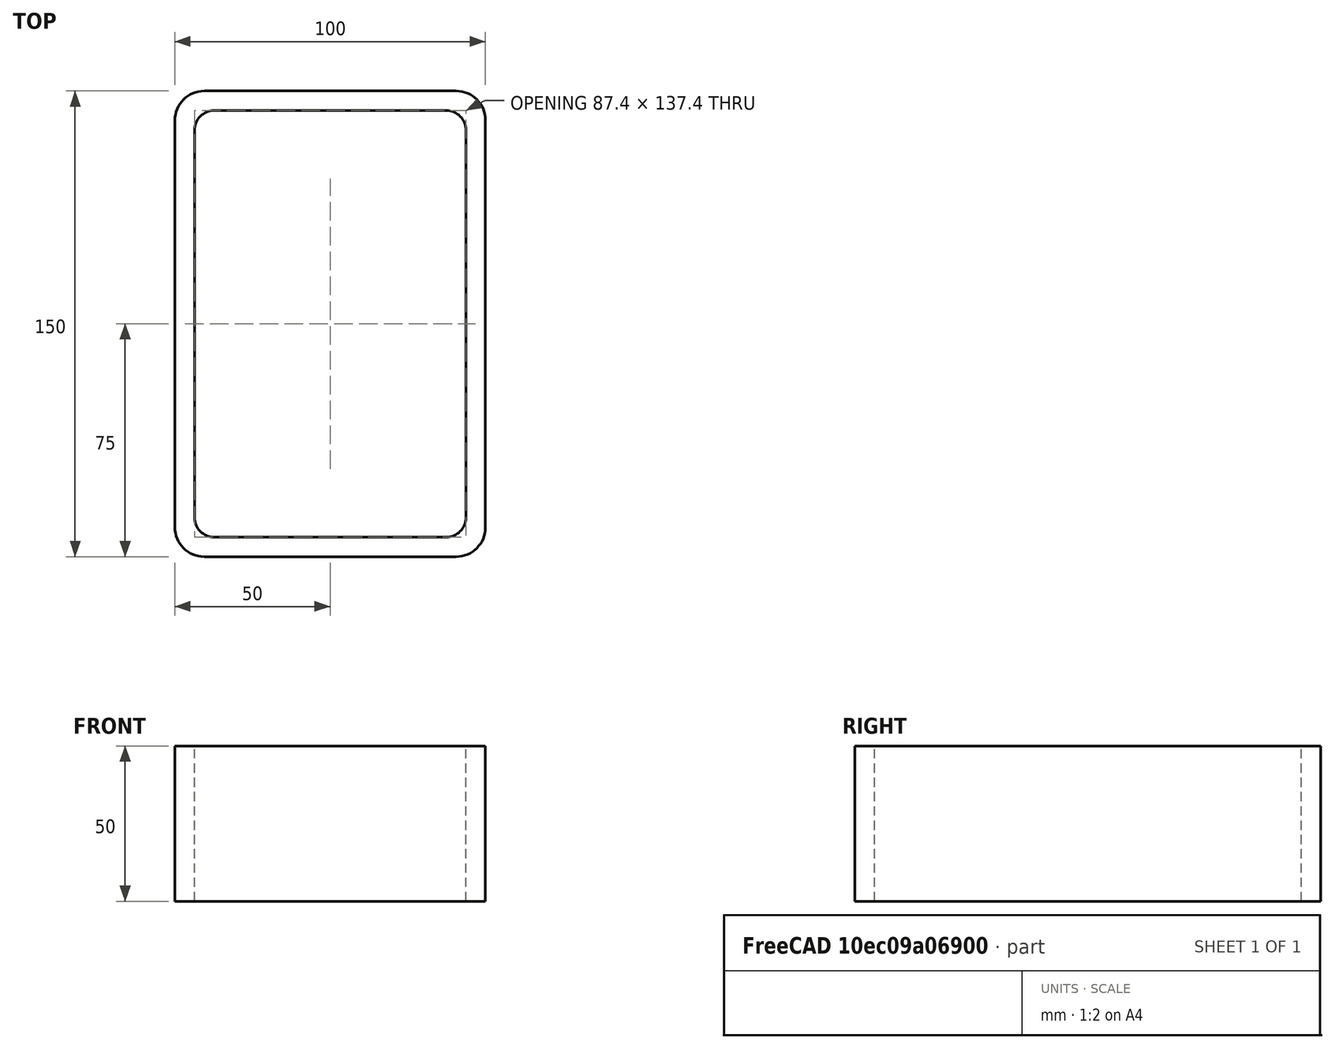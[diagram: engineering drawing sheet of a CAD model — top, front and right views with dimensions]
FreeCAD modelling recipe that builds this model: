
FCSTD DOCUMENT  (FreeCAD 0.15R4671 (Git))
Label: Rectangular hollow section 150x100x6.3 EN10219 S235JRH
License: All rights reserved
LicenseURL: http://en.wikipedia.org/wiki/All_rights_reserved
objects: Sketcher::SketchObject×1, Part::Extrusion×1
note: 2 computed .brp shape members not serialized (recipe doc carries the construction recipe); baked Part::Feature solids carry a one-line shape summary decoded from their .brp

FEATURE [Sketcher::SketchObject] Sketch
  sketch-geometry (16):
    g0: LineSegment StartX=-37.4 StartY=68.7 StartZ=0 EndX=37.4 EndY=68.7 EndZ=0
    g1: LineSegment StartX=43.7 StartY=62.4 StartZ=0 EndX=43.7 EndY=-62.4 EndZ=0
    g2: LineSegment StartX=37.4 StartY=-68.7 StartZ=0 EndX=-37.4 EndY=-68.7 EndZ=0
    g3: LineSegment StartX=-43.7 StartY=-62.4 StartZ=0 EndX=-43.7 EndY=62.4 EndZ=0
    g4: LineSegment StartX=-40.55 StartY=75 StartZ=0 EndX=40.55 EndY=75 EndZ=0
    g5: LineSegment StartX=50 StartY=65.55 StartZ=0 EndX=50 EndY=-65.55 EndZ=0
    g6: LineSegment StartX=40.55 StartY=-75 StartZ=0 EndX=-40.55 EndY=-75 EndZ=0
    g7: LineSegment StartX=-50 StartY=-65.55 StartZ=0 EndX=-50 EndY=65.55 EndZ=0
    g8: ArcOfCircle CenterX=-37.4 CenterY=62.4 CenterZ=0 NormalX=0 NormalY=0 NormalZ=1 Radius=6.3 StartAngle=1.5708 EndAngle=3.14159
    g9: ArcOfCircle CenterX=37.4 CenterY=62.4 CenterZ=0 NormalX=0 NormalY=0 NormalZ=1 Radius=6.3 StartAngle=0 EndAngle=1.5708
    g10: ArcOfCircle CenterX=37.4 CenterY=-62.4 CenterZ=0 NormalX=0 NormalY=0 NormalZ=1 Radius=6.3 StartAngle=4.71239 EndAngle=6.28319
    g11: ArcOfCircle CenterX=-37.4 CenterY=-62.4 CenterZ=0 NormalX=0 NormalY=0 NormalZ=1 Radius=6.3 StartAngle=3.14159 EndAngle=4.71239
    g12: ArcOfCircle CenterX=40.55 CenterY=65.55 CenterZ=0 NormalX=0 NormalY=0 NormalZ=1 Radius=9.45 StartAngle=0 EndAngle=1.5708
    g13: ArcOfCircle CenterX=40.55 CenterY=-65.55 CenterZ=0 NormalX=0 NormalY=0 NormalZ=1 Radius=9.45 StartAngle=4.71239 EndAngle=6.28319
    g14: ArcOfCircle CenterX=-40.55 CenterY=-65.55 CenterZ=0 NormalX=0 NormalY=0 NormalZ=1 Radius=9.45 StartAngle=3.14159 EndAngle=4.71239
    g15: ArcOfCircle CenterX=-40.55 CenterY=65.55 CenterZ=0 NormalX=0 NormalY=0 NormalZ=1 Radius=9.45 StartAngle=1.5708 EndAngle=3.14159
  constraints (36):
    c: Horizontal(g2)
    c: Vertical(g3)
    c: Horizontal(g6)
    c: Vertical(g7)
    c: Tangent(g3,g8) = 1.5708
    c: Tangent(g0,g8) = 1.5708
    c: Tangent(g0,g9) = 1.5708
    c: Tangent(g1,g9) = 1.5708
    c: Tangent(g1,g10) = 1.5708
    c: Tangent(g2,g10) = 1.5708
    c: Tangent(g2,g11) = 1.5708
    c: Tangent(g3,g11) = 1.5708
    c: Tangent(g4,g12) = 1.5708
    c: Tangent(g5,g12) = 1.5708
    c: Tangent(g5,g13) = 1.5708
    c: Tangent(g6,g13) = 1.5708
    c: Tangent(g6,g14) = 1.5708
    c: Tangent(g7,g14) = 1.5708
    c: Tangent(g7,g15) = 1.5708
    c: Tangent(g4,g15) = 1.5708
    c: Equal(g9,g8)
    c: Equal(g9,g11)
    c: Equal(g9,g10)
    c: Equal(g12,g15)
    c: Equal(g12,g14)
    c: Equal(g12,g13)
    c: Symmetric(g4,g6,g-1)
    c: Symmetric(g7,g5,g-2)
    c: DistanceY(g4,g6) = -150
    c: DistanceX(g7,g5) = 100
    c: Symmetric(g3,g1,g-2)
    c: Symmetric(g0,g2,g-1)
    c: DistanceY(g0,g4) = 6.3
    c: DistanceX(g5,g1) = -6.3
    c: Radius(g9) = 6.3
    c: Radius(g12) = 9.45
FEATURE [Part::Extrusion] Extrude  label="Rectangular hollow section 150x100x6.3 EN10219 S235JRH"
  Base = -> Sketch
  Dir = (0,0,50)
  Solid = true
